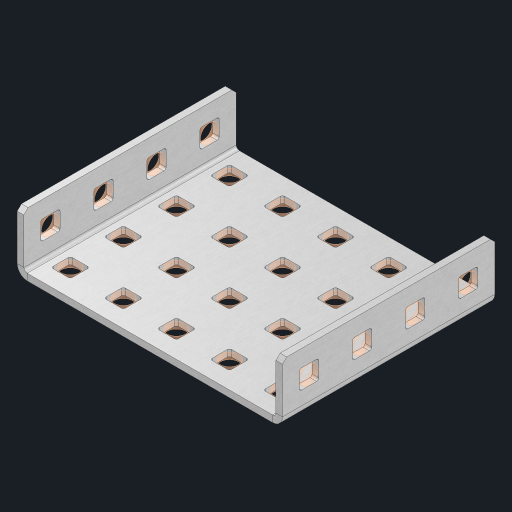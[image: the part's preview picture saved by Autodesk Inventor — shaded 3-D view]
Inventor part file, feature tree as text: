
AUTODESK INVENTOR PART (.ipt)
format: ipt  version: 2023 (Build 270158000, 158)  size: 608,768 bytes
history: native  units: in
note: dims shown in document units (in); Inventor stores cm internally (conversion verified against a paired STEP export)
features: other x33, extrude x27, sheet_metal_op x10, sketch x8, mirror x1, pattern_linear x1, chamfer x1
ambient origin geometry x8: Origin, YZ Plane, XZ Plane, XY Plane, X Axis, Y Axis, Z Axis, Center Point
bodies: Solid1 (feature_tree), Body (feature_tree)
feature tree (81):
  other  "Flange Pattern Plane"
  sheet_metal_op  "Flange Pattern"
  sheet_metal_op  "Body Pattern"
  other  "Arc Length"
  mirror  "Notch Mirror"
  pattern_linear  "Notch Pattern"  Spacing1=0.25in  [1 undecoded]
  chamfer  "End Chamfer"
  extrude  "Half Cut"  Depth=0.0625in
  sketch  "Sketch1"  dims[d0=2.5in]
  other  "Plate1"
  sketch  "Sketch2"  dims[d1=2.0in]
  other  "Plate2"
  sheet_metal_op  "Bend1"
  sheet_metal_op  "Corner1"
  sketch  "Sketch3"  dims[d2=0.0625in]
  other  "Flange Pattern Sketch"
  sketch  "Sketch7"  dims[d3=0.0625in]
  other  "Srf1"
  other  "Srf2"
  sketch  "Sketch8"  dims[d4=0.0312in]
  sketch  "Sketch9"  dims[d5=0.125in]
  other  "Srf91"
  sheet_metal_op  "Body Pattern Sketch"
  other  "Srf92"
  sketch  "Sketch13"  dims[d6=0.0625in]
  sketch  "Sketch14"  dims[d7=0.5in d8=90.0deg d9=0.0312in d10=0.25in d11=0.0625in d12=0.0625in d16=0.182in d17=0.02in d18=0.0625in d19=0.0in d20=0.25in d21=0.25in d46=0.172in d47=1.0in d48=0.0in d49=0.182in d50=0.02in d51=0.25in d52=0.25in d53=0.0625in d54=0.0in d55=0.172in d56=1.0in d57=0.0in d60=1.5748in d62=0.5in d63=1.9685in d65=0.5in d85=0.1473in d86=0.1782in d88=0.04in d89=0.0625in d90=0.0in d91=0.04in d92=0.0491in d95=2.5in d96=0.04in d97=0.25in d98=45.0deg d101=0.0in d102=2.497in d131=2.5in d132=1.5748in d134=0.5in d139=0.5in]
  other  "Srf856"
  other  "Srf1310"
  other  "Srf1311"
  other  "Srf1312"
  other  "Srf1376"
  other  "Srf1377"
  other  "Srf1728"
  other  "Srf1755"
  other  "Srf1878"
  other  "Srf1879"
  other  "Srf1942"
  other  "Srf1943"
  other  "Srf1944"
  other  "Srf1945"
  other  "Srf1946"
  other  "Srf1947"
  other  "Srf1948"
  other  "Srf1949"
  other  "Srf1950"
  other  "Srf1951"
  other  "Srf1952"
  other  "Srf1953"
  other  "Srf1954"
  other  "Srf1955"
  sheet_metal_op  "Flange Stamp"
  sheet_metal_op  "Flange Circle"
  sheet_metal_op  "Body Stamp"
  sheet_metal_op  "Body Circle"
  sheet_metal_op  "Notch"
  extrude  "ExtrusionSrf2"  Depth=0.0625in
  extrude  "ExtrusionSrf92"  Depth=0.182in
  extrude  "ExtrusionSrf856"  Depth=0.02in
  extrude  "ExtrusionSrf1310"  Depth=0.0625in
  extrude  "ExtrusionSrf1311"  TaperAngle=0.0deg  [1 undecoded]
  extrude  "ExtrusionSrf1312"  Depth=0.25in
  extrude  "ExtrusionSrf1376"  Depth=0.25in
  extrude  "ExtrusionSrf1377"  Depth=0.5in
  extrude  "ExtrusionSrf1728"  Depth=1.0in TaperAngle=0.0deg
  extrude  "ExtrusionSrf1755"  Depth=0.182in
  extrude  "ExtrusionSrf1878"  Depth=0.02in
  extrude  "ExtrusionSrf1879"  Depth=0.25in
  extrude  "ExtrusionSrf1942"  Depth=0.25in
  extrude  "ExtrusionSrf1943"  Depth=0.0625in
  extrude  "ExtrusionSrf1944"  TaperAngle=0.0deg  [1 undecoded]
  extrude  "ExtrusionSrf1945"  Depth=0.5in
  extrude  "ExtrusionSrf1946"  Depth=1.0in TaperAngle=0.0deg
  extrude  "ExtrusionSrf1947"  Depth=0.5in
  extrude  "ExtrusionSrf1948"  Depth=0.5in
  extrude  "ExtrusionSrf1949"  Depth=0.5in
  extrude  "ExtrusionSrf1950"  Depth=0.5in
  extrude  "ExtrusionSrf1951"  Depth=0.5in
  extrude  "ExtrusionSrf1952"  Depth=0.0625in
  extrude  "ExtrusionSrf1953"  TaperAngle=0.0deg  [1 undecoded]
  extrude  "ExtrusionSrf1954"  Depth=0.5in
  extrude  "ExtrusionSrf1955"  Depth=0.5in
note: 4 required parameter values undecoded (feature->parameter linkage not recoverable at this tier; creation-order binding heuristic only, values carry confidence <= 0.55)
